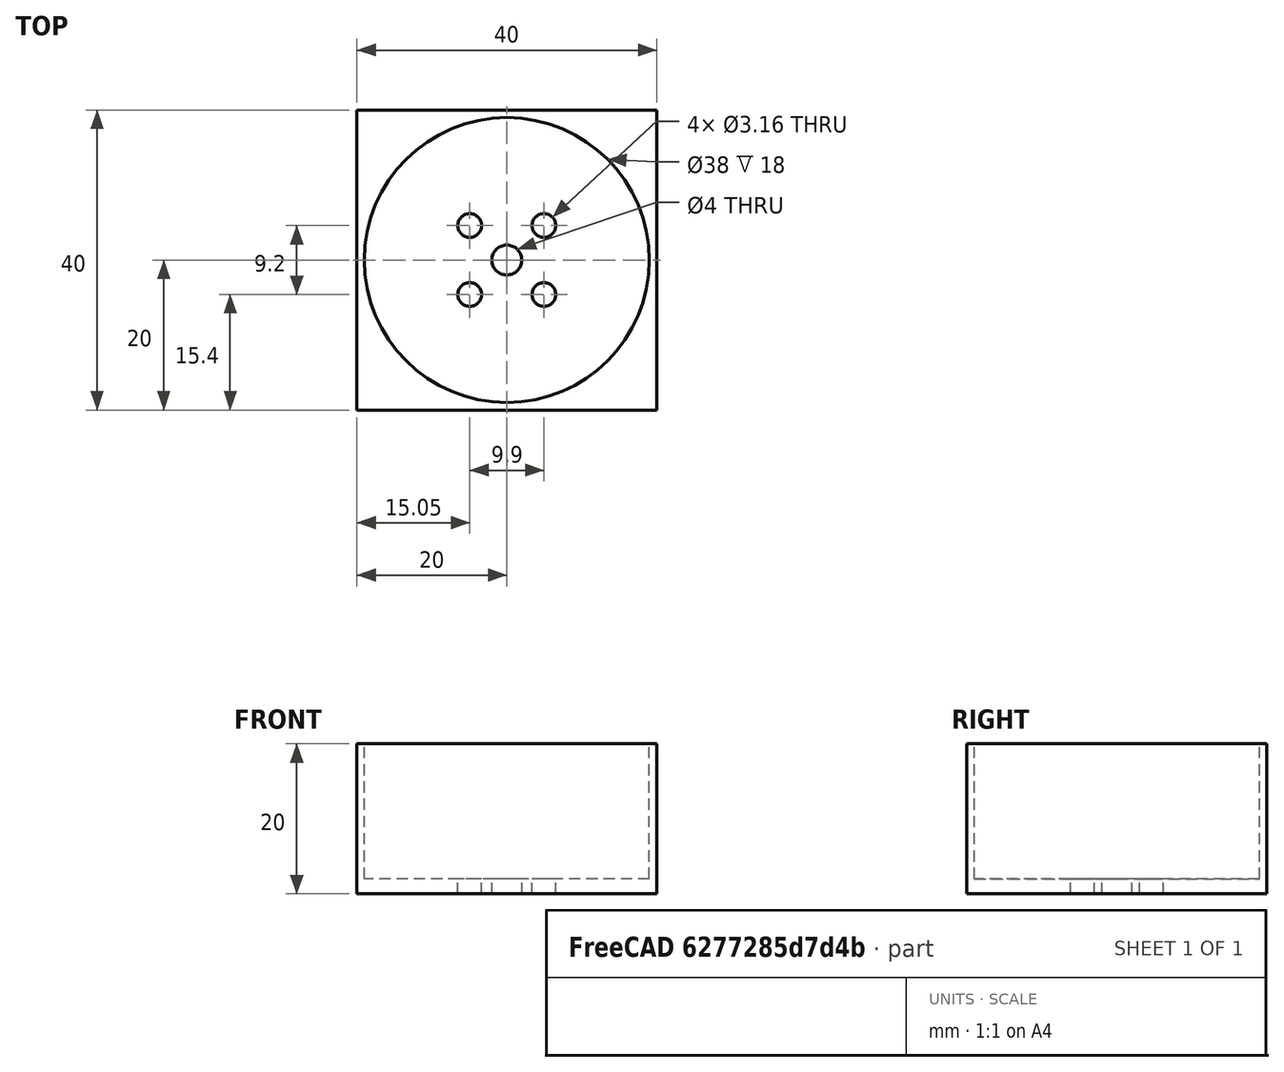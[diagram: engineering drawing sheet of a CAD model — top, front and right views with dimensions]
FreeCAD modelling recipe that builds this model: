
FCSTD DOCUMENT  (FreeCAD 0.16R)
Label: Jig
License: All rights reserved
LicenseURL: http://en.wikipedia.org/wiki/All_rights_reserved
objects: Part::Cylinder×6, Part::Cut×6, Part::Box×1
note: 13 computed .brp shape members not serialized (recipe doc carries the construction recipe); baked Part::Feature solids carry a one-line shape summary decoded from their .brp

FEATURE [Part::Box] Box  label="Cube"
  Height = 20
  Length = 40
  Placement = pos=(-20,-20,-2) rot=(0,0,1;0rad)
  Width = 40
FEATURE [Part::Cylinder] Cylinder
  Angle = 360
  Height = 19
  Radius = 19
FEATURE [Part::Cut] Cut
  Base = -> Box
  Tool = -> Cylinder
FEATURE [Part::Cylinder] Cylinder001
  Angle = 360
  Height = 20
  Placement = pos=(0,0,-2) rot=(0,0,1;0rad)
  Radius = 2
FEATURE [Part::Cylinder] Cylinder002
  Angle = 360
  Height = 20
  Placement = pos=(-4.95,4.6,-2) rot=(0,0,1;0rad)
  Radius = 1.58
FEATURE [Part::Cylinder] Cylinder003
  Angle = 360
  Height = 20
  Placement = pos=(4.95,-4.6,-2) rot=(0,0,1;0rad)
  Radius = 1.58
FEATURE [Part::Cylinder] Cylinder004
  Angle = 360
  Height = 20
  Placement = pos=(-4.95,-4.6,-2) rot=(0,0,1;0rad)
  Radius = 1.58
FEATURE [Part::Cut] Cut001
  Base = -> Cut
  Tool = -> Cylinder004
FEATURE [Part::Cut] Cut002
  Base = -> Cut001
  Tool = -> Cylinder003
FEATURE [Part::Cut] Cut003
  Base = -> Cut002
  Tool = -> Cylinder002
FEATURE [Part::Cut] Cut004
  Base = -> Cut003
  Tool = -> Cylinder001
FEATURE [Part::Cylinder] Cylinder005
  Angle = 360
  Height = 20
  Placement = pos=(4.95,4.6,-2) rot=(0,0,1;0rad)
  Radius = 1.58
FEATURE [Part::Cut] Cut005
  Base = -> Cut004
  Tool = -> Cylinder005
